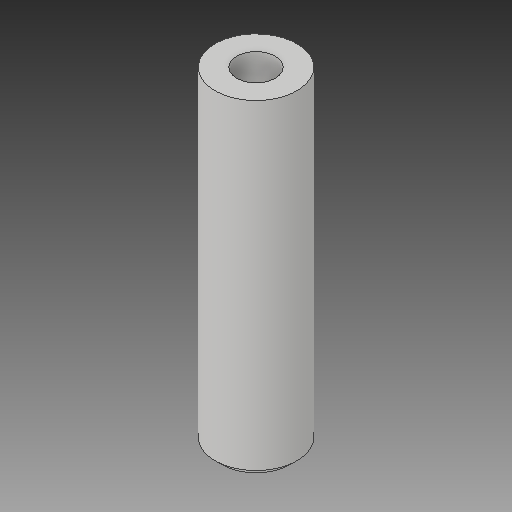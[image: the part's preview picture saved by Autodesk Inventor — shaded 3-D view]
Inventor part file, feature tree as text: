
AUTODESK INVENTOR PART (.ipt)
format: ipt  version: 2018 (Build 220112000, 112)  size: 98,816 bytes
history: native  units: mm
features: extrude x1, chamfer x1, sketch x1
ambient origin geometry x8: Origin, YZ Plane, XZ Plane, XY Plane, X Axis, Y Axis, Z Axis, Center Point
bodies: Solid1 (feature_tree)
feature tree (3):
  extrude  "Extrusion1"  Depth=2.0mm
  chamfer  "Chamfer1"  Distance=200.0mm
  sketch  "Sketch1"  dims[d0=50.0mm d1=23.5mm d2=200.0mm d3=0.0mm d4=4.0mm d5=2.0mm d6=45.0deg]
